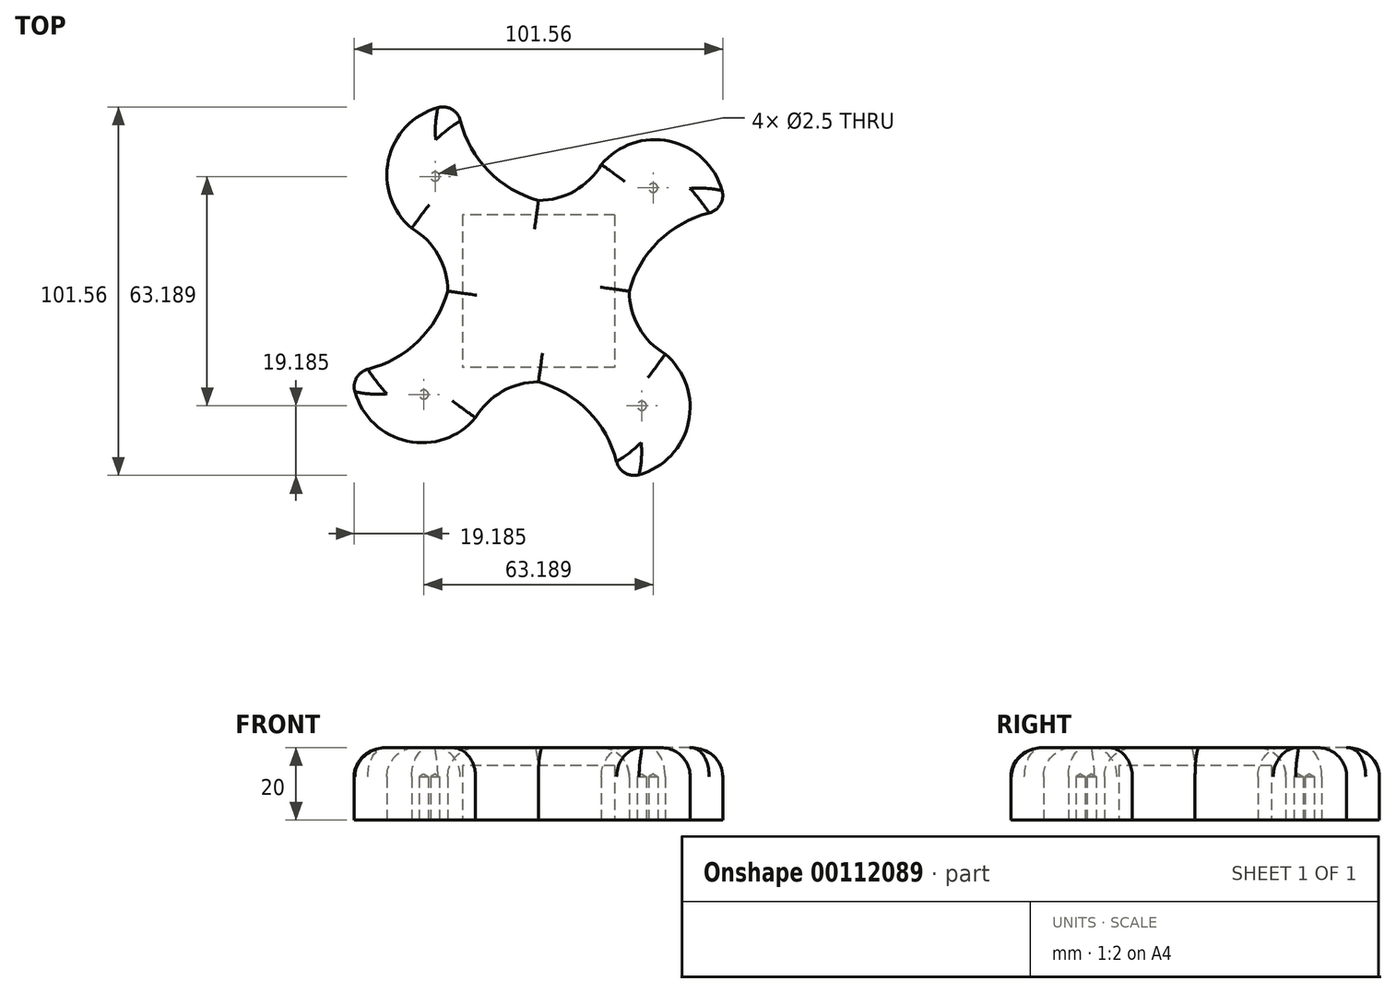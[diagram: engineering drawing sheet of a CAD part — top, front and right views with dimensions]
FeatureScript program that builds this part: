
annotation { "Feature Type Name" : "Feature", "Feature Type Description" : "" }
export const myFeature = defineFeature(function(context is Context, id is Id, definition is map)
    precondition{}
    {
        {
            var Q0;
            Q0=qCreatedBy(makeId("Top.planeOp"),FACE);
            var sketch = newSketch(context, id + "F0", { "sketchPlane" : qUnion([Q0])});
            skPoint(sketch, "E0.middle", {"position": v(0, 0) * mm});
            skArc(sketch, "E1", {"start": v(-22.28, 51.3) * mm, "mid": v(-40.57, 38.77) * mm, "end": v(-34.9, 17.33) * mm});
            skPoint(sketch, "E2", {"position": v(-45.11, 0) * mm});
            skArc(sketch, "E3", {"start": v(-34.9, 17.33) * mm, "mid": v(-27.65, 9.98) * mm, "end": v(-25, 0) * mm});
            skArc(sketch, "E4", {"start": v(-22.28, 51.3) * mm, "mid": v(-15.21, 34.7) * mm, "end": v(0, 25) * mm});
            skArc(sketch, "E5.1.0", {"start": v(-51.3, -22.28) * mm, "mid": v(-38.77, -40.57) * mm, "end": v(-17.33, -34.9) * mm});
            skArc(sketch, "E5.1.1", {"start": v(-51.3, -22.28) * mm, "mid": v(-34.7, -15.21) * mm, "end": v(-25, 0) * mm});
            skArc(sketch, "E5.1.2", {"start": v(-17.33, -34.9) * mm, "mid": v(-9.98, -27.65) * mm, "end": v(0, -25) * mm});
            skArc(sketch, "E5.2.0", {"start": v(22.28, -51.3) * mm, "mid": v(40.57, -38.77) * mm, "end": v(34.9, -17.33) * mm});
            skArc(sketch, "E5.2.1", {"start": v(22.28, -51.3) * mm, "mid": v(15.21, -34.7) * mm, "end": v(0, -25) * mm});
            skArc(sketch, "E5.2.2", {"start": v(34.9, -17.33) * mm, "mid": v(27.65, -9.98) * mm, "end": v(25, 0) * mm});
            skArc(sketch, "E5.3.0", {"start": v(51.3, 22.28) * mm, "mid": v(38.77, 40.57) * mm, "end": v(17.33, 34.9) * mm});
            skArc(sketch, "E5.3.1", {"start": v(51.3, 22.28) * mm, "mid": v(34.7, 15.21) * mm, "end": v(25, 0) * mm});
            skArc(sketch, "E5.3.2", {"start": v(17.33, 34.9) * mm, "mid": v(9.98, 27.65) * mm, "end": v(0, 25) * mm});
            skSolve(sketch);
        }
        {
            var Q0;
            Q0=makeQuery(id+"F0.imprint","IMPRINT",FACE,{"disambiguationData":[TD([[makeQuery(id+"F0.imprint","IMPRINT",EDGE,{"derivedFrom":sQuery(id+"F0.wireOp",EDGE,"E1")}),1.0]])]});
            extrude(context, id + "F1", {"entities" : qUnion([Q0]), "depth" : 20 * mm});
        }
        {
            var Q0;
            Q0=makeQuery(id+"F1.opExtrude","CAP_EDGE",EDGE,{"disambiguationData":[OSD([sQuery(id+"F0.wireOp",EDGE,"E5.1.1")])],"isStart":false});
            var Q1;
            Q1=makeQuery(id+"F1.opExtrude","CAP_EDGE",EDGE,{"disambiguationData":[OSD([sQuery(id+"F0.wireOp",EDGE,"E1")])],"isStart":false});
            var Q2;
            Q2=makeQuery(id+"F1.opExtrude","CAP_EDGE",EDGE,{"disambiguationData":[OSD([sQuery(id+"F0.wireOp",EDGE,"E3")])],"isStart":false});
            var Q3;
            Q3=makeQuery(id+"F1.opExtrude","CAP_EDGE",EDGE,{"disambiguationData":[OSD([sQuery(id+"F0.wireOp",EDGE,"E5.2.1")])],"isStart":false});
            var Q4;
            Q4=makeQuery(id+"F1.opExtrude","CAP_EDGE",EDGE,{"disambiguationData":[OSD([sQuery(id+"F0.wireOp",EDGE,"E5.1.2")])],"isStart":false});
            var Q5;
            Q5=makeQuery(id+"F1.opExtrude","CAP_EDGE",EDGE,{"disambiguationData":[OSD([sQuery(id+"F0.wireOp",EDGE,"E5.1.0")])],"isStart":false});
            var Q6;
            Q6=makeQuery(id+"F1.opExtrude","CAP_EDGE",EDGE,{"disambiguationData":[OSD([sQuery(id+"F0.wireOp",EDGE,"E5.2.0")])],"isStart":false});
            var Q7;
            Q7=makeQuery(id+"F1.opExtrude","CAP_EDGE",EDGE,{"disambiguationData":[OSD([sQuery(id+"F0.wireOp",EDGE,"E5.2.2")])],"isStart":false});
            var Q8;
            Q8=makeQuery(id+"F1.opExtrude","CAP_EDGE",EDGE,{"disambiguationData":[OSD([sQuery(id+"F0.wireOp",EDGE,"E5.3.1")])],"isStart":false});
            var Q9;
            Q9=makeQuery(id+"F1.opExtrude","CAP_EDGE",EDGE,{"disambiguationData":[OSD([sQuery(id+"F0.wireOp",EDGE,"E5.3.0")])],"isStart":false});
            var Q10;
            Q10=makeQuery(id+"F1.opExtrude","CAP_EDGE",EDGE,{"disambiguationData":[OSD([sQuery(id+"F0.wireOp",EDGE,"E5.3.2")])],"isStart":false});
            var Q11;
            Q11=makeQuery(id+"F1.opExtrude","CAP_EDGE",EDGE,{"disambiguationData":[OSD([sQuery(id+"F0.wireOp",EDGE,"E4")])],"isStart":false});
            fillet(context, id + "F2", {"entities" : qUnion([Q0, Q1, Q2, Q3, Q4, Q5, Q6, Q7, Q8, Q9, Q10, Q11]), "radius" : 8 * mm, "allowEdgeOverflow" : false});
        }
        {
            var Q0;
            Q0=makeQuery(id+"F1.opExtrude","SWEPT_EDGE",EDGE,{"disambiguationData":[OSD([sQuery(id+"F0.wireOp",EDGE,"E5.2.0"),sQuery(id+"F0.wireOp",EDGE,"E5.2.1")])]});
            var Q1;
            Q1=makeQuery(id+"F1.opExtrude","SWEPT_EDGE",EDGE,{"disambiguationData":[OSD([sQuery(id+"F0.wireOp",EDGE,"E5.1.0"),sQuery(id+"F0.wireOp",EDGE,"E5.1.1")])]});
            var Q2;
            Q2=makeQuery(id+"F1.opExtrude","SWEPT_EDGE",EDGE,{"disambiguationData":[OSD([sQuery(id+"F0.wireOp",EDGE,"E1"),sQuery(id+"F0.wireOp",EDGE,"E4")])]});
            var Q3;
            Q3=makeQuery(id+"F1.opExtrude","SWEPT_EDGE",EDGE,{"disambiguationData":[OSD([sQuery(id+"F0.wireOp",EDGE,"E5.3.0"),sQuery(id+"F0.wireOp",EDGE,"E5.3.1")])]});
            fillet(context, id + "F3", {"entities" : qUnion([Q0, Q1, Q2, Q3]), "radius" : 5 * mm, "tangentPropagation" : true, "allowEdgeOverflow" : false});
        }
        {
            var Q0;
            Q0=qCreatedBy(makeId("Top.planeOp"),FACE);
            var sketch = newSketch(context, id + "F4", { "sketchPlane" : qUnion([Q0])});
            skLineSegment(sketch, "E6.bottom", {"start": v(21, 21) * mm, "end": v(-21, 21) * mm});
            skLineSegment(sketch, "E6.top", {"start": v(21, -21) * mm, "end": v(-21, -21) * mm});
            skLineSegment(sketch, "E6.left", {"start": v(21, 21) * mm, "end": v(21, -21) * mm});
            skLineSegment(sketch, "E6.right", {"start": v(-21, 21) * mm, "end": v(-21, -21) * mm});
            skPoint(sketch, "E6.middle", {"position": v(0, 0) * mm});
            skCircle(sketch, "E7", {"center": v(-28.49, 31.6) * mm, "radius": 1.25 * mm});
            skCircle(sketch, "E8.1.0", {"center": v(-31.6, -28.49) * mm, "radius": 1.25 * mm});
            skCircle(sketch, "E8.2.0", {"center": v(28.49, -31.6) * mm, "radius": 1.25 * mm});
            skCircle(sketch, "E8.3.0", {"center": v(31.6, 28.49) * mm, "radius": 1.25 * mm});
            skSolve(sketch);
        }
        {
            var Q0;
            Q0=makeQuery(id+"F4.imprint","IMPRINT",FACE,{"disambiguationData":[TD([[makeQuery(id+"F4.imprint","IMPRINT",EDGE,{"derivedFrom":sQuery(id+"F4.wireOp",EDGE,"E6.bottom")}),1.0]])]});
            extrude(context, id + "F5", {"entities" : qUnion([Q0]), "depth" : 15 * mm});
        }
        {
            var Q0;
            Q0=makeQuery(id+"F5.opExtrude","SWEPT_BODY",BODY,{"disambiguationData":[OSD([sQuery(id+"F4.wireOp",EDGE,"E6.bottom"),sQuery(id+"F4.wireOp",EDGE,"E6.top"),sQuery(id+"F4.wireOp",EDGE,"E6.left"),sQuery(id+"F4.wireOp",EDGE,"E6.right")])]});
            var Q1;
            Q1=makeQuery(id+"F1.opExtrude","SWEPT_BODY",BODY,{"disambiguationData":[OSD([sQuery(id+"F0.wireOp",EDGE,"E1"),sQuery(id+"F0.wireOp",EDGE,"E3"),sQuery(id+"F0.wireOp",EDGE,"E4"),sQuery(id+"F0.wireOp",EDGE,"E5.1.0"),sQuery(id+"F0.wireOp",EDGE,"E5.1.1"),sQuery(id+"F0.wireOp",EDGE,"E5.1.2"),sQuery(id+"F0.wireOp",EDGE,"E5.2.0"),sQuery(id+"F0.wireOp",EDGE,"E5.2.1"),sQuery(id+"F0.wireOp",EDGE,"E5.2.2"),sQuery(id+"F0.wireOp",EDGE,"E5.3.0"),sQuery(id+"F0.wireOp",EDGE,"E5.3.1"),sQuery(id+"F0.wireOp",EDGE,"E5.3.2")])]});
            booleanBodies(context, id + "F6", {"operationType" : BooleanOperationType.SUBTRACTION, "tools" : qUnion([Q0]), "targets" : qUnion([Q1])});
        }
        {
            var Q0;
            Q0=sQuery(id+"F4.wireOp",VERTEX,"E8.1.0.center");
            var Q1;
            Q1=sQuery(id+"F4.wireOp",VERTEX,"E7.center");
            var Q2;
            Q2=sQuery(id+"F4.wireOp",VERTEX,"E8.2.0.center");
            var Q3;
            Q3=sQuery(id+"F4.wireOp",VERTEX,"E8.3.0.center");
            var Q4;
            Q4=makeQuery(id+"F1.opExtrude","SWEPT_BODY",BODY,{"disambiguationData":[OSD([sQuery(id+"F0.wireOp",EDGE,"E1"),sQuery(id+"F0.wireOp",EDGE,"E3"),sQuery(id+"F0.wireOp",EDGE,"E4"),sQuery(id+"F0.wireOp",EDGE,"E5.1.0"),sQuery(id+"F0.wireOp",EDGE,"E5.1.1"),sQuery(id+"F0.wireOp",EDGE,"E5.1.2"),sQuery(id+"F0.wireOp",EDGE,"E5.2.0"),sQuery(id+"F0.wireOp",EDGE,"E5.2.1"),sQuery(id+"F0.wireOp",EDGE,"E5.2.2"),sQuery(id+"F0.wireOp",EDGE,"E5.3.0"),sQuery(id+"F0.wireOp",EDGE,"E5.3.1"),sQuery(id+"F0.wireOp",EDGE,"E5.3.2")])]});
            hole(context, id + "F7", {"style" : HoleStyle.SIMPLE, "endStyle" : HoleEndStyle.BLIND, "oppositeDirection" : true, "holeDiameter" : 2.5 * mm, "holeDepth" : 12 * mm, "locations" : qUnion([Q0, Q1, Q2, Q3]), "scope" : qUnion([Q4])});
        }
    });
